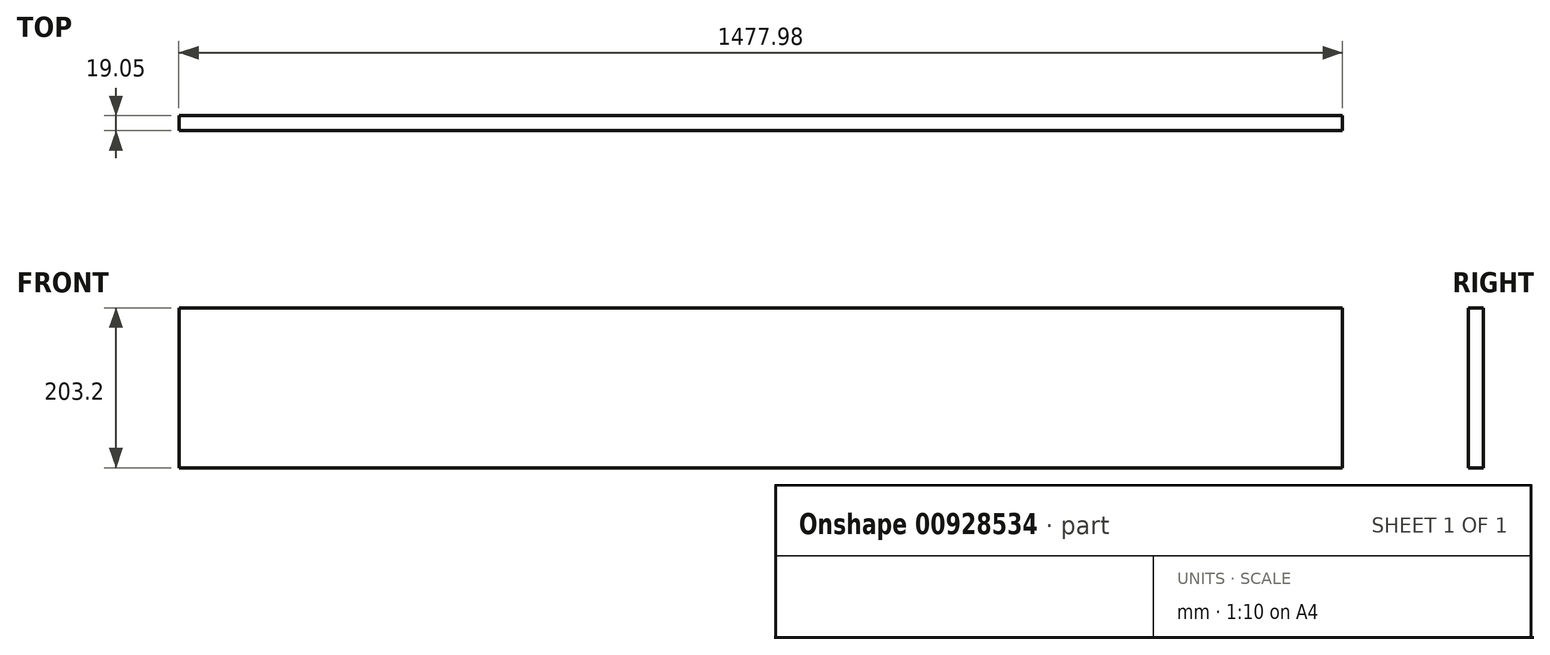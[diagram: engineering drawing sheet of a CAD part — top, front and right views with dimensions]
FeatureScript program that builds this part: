
annotation { "Feature Type Name" : "Feature", "Feature Type Description" : "" }
export const myFeature = defineFeature(function(context is Context, id is Id, definition is map)
    precondition{}
    {
        {
            var Q0;
            Q0=qCreatedBy(makeId("Front.planeOp"),FACE);
            var sketch = newSketch(context, id + "F0", { "sketchPlane" : qUnion([Q0])});
            skLineSegment(sketch, "E0.bottom", {"start": v(-738.99, 101.6) * mm, "end": v(738.99, 101.6) * mm});
            skLineSegment(sketch, "E0.top", {"start": v(-738.99, -101.6) * mm, "end": v(738.99, -101.6) * mm});
            skLineSegment(sketch, "E0.left", {"start": v(-738.99, 101.6) * mm, "end": v(-738.99, -101.6) * mm});
            skLineSegment(sketch, "E0.right", {"start": v(738.99, 101.6) * mm, "end": v(738.99, -101.6) * mm});
            skPoint(sketch, "E0.middle", {"position": v(0, 0) * mm});
            skSolve(sketch);
        }
        {
            var Q0;
            Q0=makeQuery(id+"F0.imprint","IMPRINT",FACE,{"disambiguationData":[TD([[makeQuery(id+"F0.imprint","IMPRINT",EDGE,{"derivedFrom":sQuery(id+"F0.wireOp",EDGE,"E0.bottom")}),-1.0]])]});
            extrude(context, id + "F1", {"entities" : qUnion([Q0]), "depth" : 19.05 * mm, "offsetDistance" : 25.4 * mm});
        }
    });
